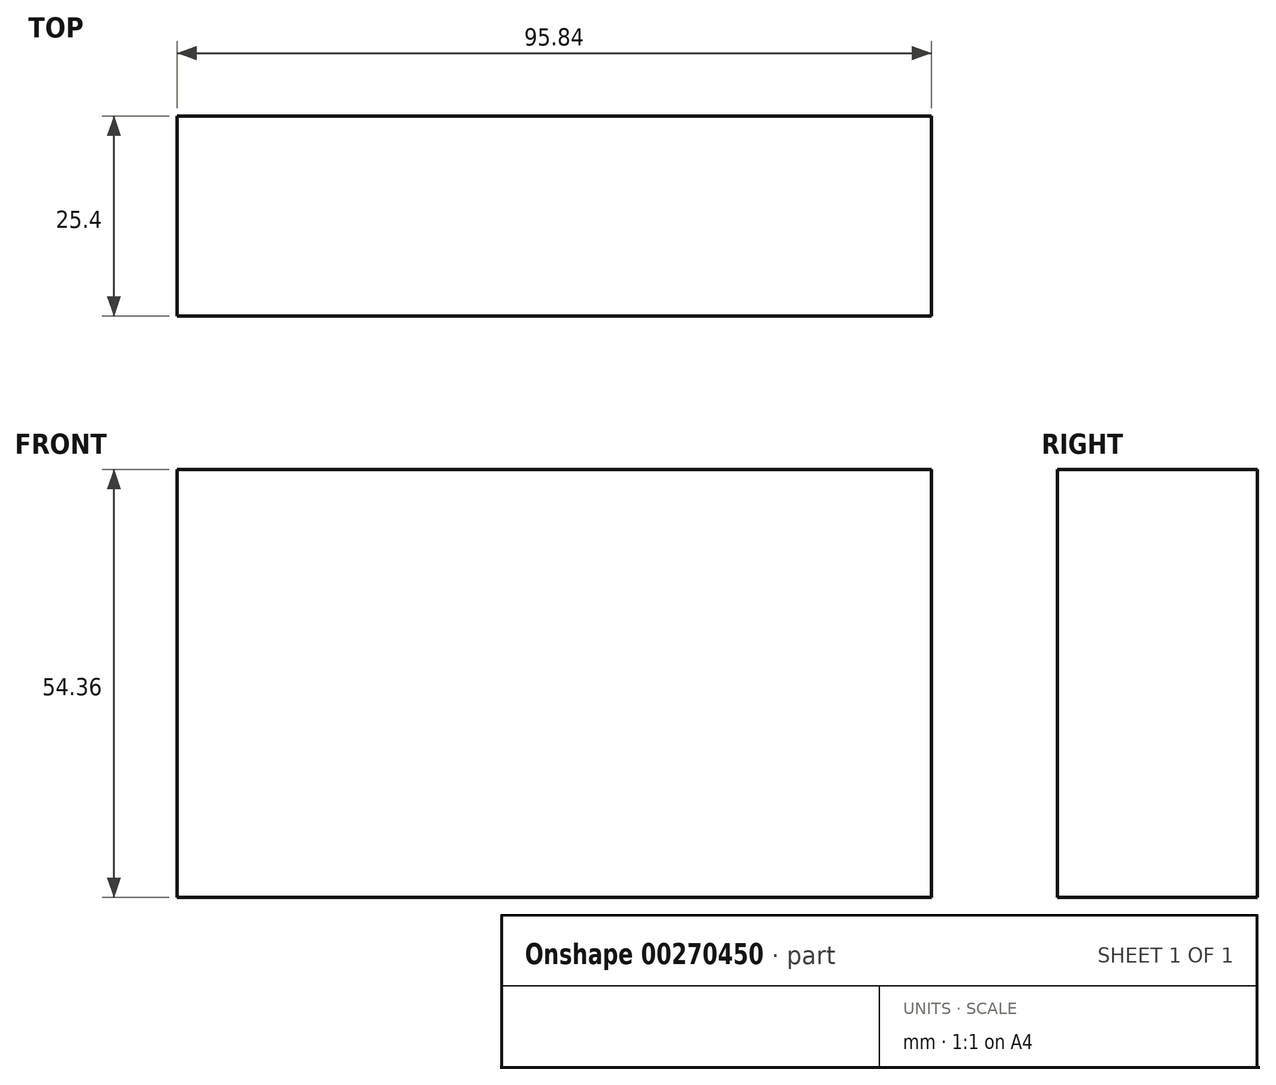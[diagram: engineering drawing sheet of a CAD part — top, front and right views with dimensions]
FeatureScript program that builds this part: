
annotation { "Feature Type Name" : "Feature", "Feature Type Description" : "" }
export const myFeature = defineFeature(function(context is Context, id is Id, definition is map)
    precondition{}
    {
        {
            var Q0;
            Q0=qCreatedBy(makeId("Front.planeOp"),FACE);
            var sketch = newSketch(context, id + "F0", { "sketchPlane" : qUnion([Q0])});
            skLineSegment(sketch, "E0.bottom", {"start": v(-47.92, 27.18) * mm, "end": v(47.92, 27.18) * mm});
            skLineSegment(sketch, "E0.top", {"start": v(-47.92, -27.18) * mm, "end": v(47.92, -27.18) * mm});
            skLineSegment(sketch, "E0.left", {"start": v(-47.92, 27.18) * mm, "end": v(-47.92, -27.18) * mm});
            skLineSegment(sketch, "E0.right", {"start": v(47.92, 27.18) * mm, "end": v(47.92, -27.18) * mm});
            skPoint(sketch, "E0.middle", {"position": v(0, 0) * mm});
            skLineSegment(sketch, "E1.bottom", {"start": v(-63.36, 41.67) * mm, "end": v(63.36, 41.67) * mm});
            skLineSegment(sketch, "E1.top", {"start": v(-63.36, -41.67) * mm, "end": v(63.36, -41.67) * mm});
            skLineSegment(sketch, "E1.left", {"start": v(-63.36, 41.67) * mm, "end": v(-63.36, -41.67) * mm});
            skLineSegment(sketch, "E1.right", {"start": v(63.36, 41.67) * mm, "end": v(63.36, -41.67) * mm});
            skLineSegment(sketch, "E2.bottom", {"start": v(-34.37, 41.67) * mm, "end": v(42.5, 41.67) * mm});
            skLineSegment(sketch, "E2.top", {"start": v(-34.37, 69.06) * mm, "end": v(42.5, 69.06) * mm});
            skLineSegment(sketch, "E2.left", {"start": v(-34.37, 41.67) * mm, "end": v(-34.37, 69.06) * mm});
            skLineSegment(sketch, "E2.right", {"start": v(42.5, 41.67) * mm, "end": v(42.5, 69.06) * mm});
            skSolve(sketch);
        }
        {
            var Q0;
            Q0=makeQuery(id+"F0.imprint","IMPRINT",FACE,{"disambiguationData":[TD([[makeQuery(id+"F0.imprint","IMPRINT",EDGE,{"derivedFrom":sQuery(id+"F0.wireOp",EDGE,"E0.bottom")}),-1.0]])]});
            extrude(context, id + "F1", {"entities" : qUnion([Q0]), "depth" : 25.4 * mm});
        }
    });
